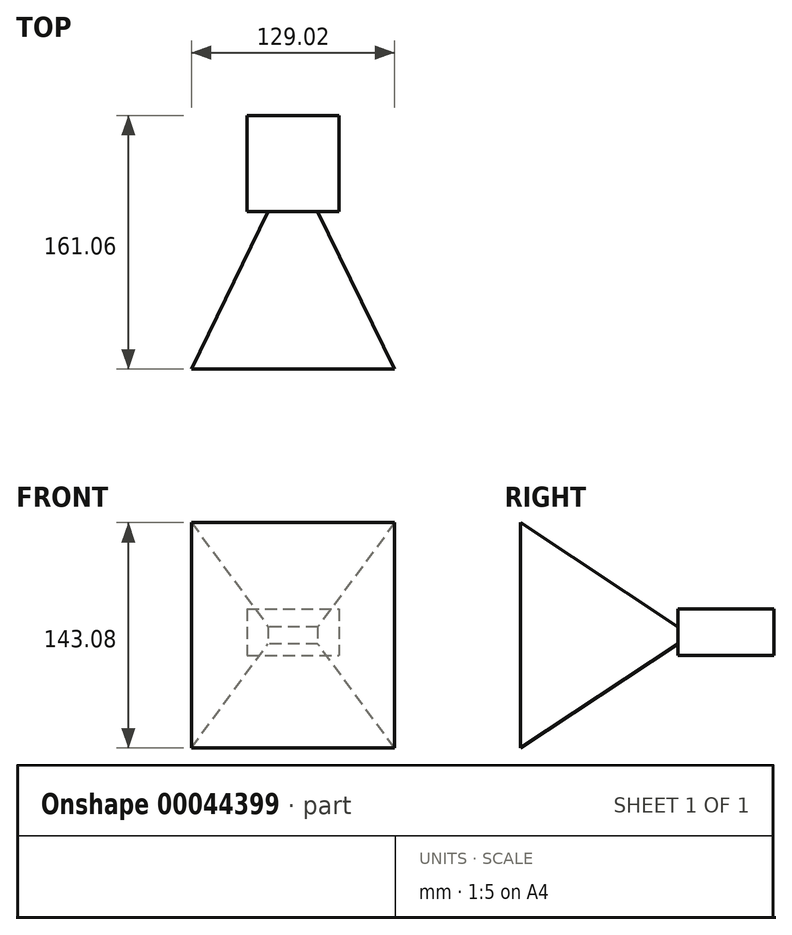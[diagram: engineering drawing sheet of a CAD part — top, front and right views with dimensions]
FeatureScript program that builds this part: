
annotation { "Feature Type Name" : "Feature", "Feature Type Description" : "" }
export const myFeature = defineFeature(function(context is Context, id is Id, definition is map)
    precondition{}
    {
        {
            var Q0;
            Q0=qCreatedBy(makeId("Top.planeOp"),FACE);
            cPlane(context, id + "F0", {"entities" : qUnion([Q0]), "cplaneType" : CPlaneType.OFFSET, "offset" : 12.64 * mm, "oppositeDirection" : true, "width" : 150 * mm, "height" : 150 * mm});
        }
        {
            var Q0;
            Q0=qCreatedBy(id+"F0.planeOp",FACE);
            var sketch = newSketch(context, id + "F1", { "sketchPlane" : qUnion([Q0])});
            skCircle(sketch, "E0", {"center": v(-15.77, 46.69) * mm, "radius": 1.5 * mm});
            skCircle(sketch, "E1", {"center": v(15.73, 16.46) * mm, "radius": 1.5 * mm});
            skLineSegment(sketch, "E2.bottom", {"start": v(-29.16, 61.06) * mm, "end": v(29.16, 61.06) * mm});
            skLineSegment(sketch, "E2.top", {"start": v(-29.16, 0) * mm, "end": v(29.16, 0) * mm});
            skLineSegment(sketch, "E2.left", {"start": v(-29.16, 61.06) * mm, "end": v(-29.16, 0) * mm});
            skLineSegment(sketch, "E2.right", {"start": v(29.16, 61.06) * mm, "end": v(29.16, 0) * mm});
            skPoint(sketch, "E3", {"position": v(0, 0) * mm});
            skSolve(sketch);
        }
        {
            var Q0;
            Q0=makeQuery(id+"F1.imprint","IMPRINT",FACE,{"disambiguationData":[TD([[makeQuery(id+"F1.imprint","IMPRINT",EDGE,{"derivedFrom":sQuery(id+"F1.wireOp",EDGE,"E0")}),-1.0]])]});
            var Q1;
            Q1=makeQuery(id+"F1.imprint","IMPRINT",FACE,{"disambiguationData":[TD([[makeQuery(id+"F1.imprint","IMPRINT",EDGE,{"derivedFrom":sQuery(id+"F1.wireOp",EDGE,"E0")}),1.0]])]});
            var Q2;
            Q2=makeQuery(id+"F1.imprint","IMPRINT",FACE,{"disambiguationData":[TD([[makeQuery(id+"F1.imprint","IMPRINT",EDGE,{"derivedFrom":sQuery(id+"F1.wireOp",EDGE,"E1")}),1.0]])]});
            extrude(context, id + "F2", {"entities" : qUnion([Q0, Q1, Q2]), "depth" : 29.4 * mm});
        }
        {
            var Q0;
            Q0=makeQuery(id+"F2.opExtrude","SWEPT_FACE",FACE,{"disambiguationData":[OSD([sQuery(id+"F1.wireOp",EDGE,"E2.top")])]});
            var sketch = newSketch(context, id + "F3", { "sketchPlane" : qUnion([Q0])});
            skLineSegment(sketch, "E4.rect.bottom", {"start": v(15.73, 5.35) * mm, "end": v(-15.73, 5.35) * mm});
            skLineSegment(sketch, "E4.rect.top", {"start": v(15.73, -5.35) * mm, "end": v(-15.73, -5.35) * mm});
            skLineSegment(sketch, "E4.rect.left", {"start": v(15.73, 5.35) * mm, "end": v(15.73, -5.35) * mm});
            skLineSegment(sketch, "E4.rect.right", {"start": v(-15.73, 5.35) * mm, "end": v(-15.73, -5.35) * mm});
            skPoint(sketch, "E4.rect.middle", {"position": v(0, 0) * mm});
            skSolve(sketch);
        }
        {
            var Q0;
            Q0=makeQuery(id+"F2.opExtrude","CAP_FACE",FACE,{"disambiguationData":[OSD([sQuery(id+"F1.wireOp",EDGE,"E0"),sQuery(id+"F1.wireOp",EDGE,"E1"),sQuery(id+"F1.wireOp",EDGE,"E2.bottom"),sQuery(id+"F1.wireOp",EDGE,"E2.top"),sQuery(id+"F1.wireOp",EDGE,"E2.left"),sQuery(id+"F1.wireOp",EDGE,"E2.right")])],"isStart":false});
            var sketch = newSketch(context, id + "F4", { "sketchPlane" : qUnion([Q0])});
            skText(sketch, "E5", { "text": "this is \nthe bottom.", "fontName": "OpenSans-Regular.ttf"});
            const initialGuessF4  = {"E5": [-0.01787, 0.03768, 1, 0, 0.0049]};
            skSetInitialGuess(sketch, initialGuessF4);
            skSolve(sketch);
        }
        {
            var Q0;
            Q0=qCreatedBy(makeId("Front.planeOp"),FACE);
            cPlane(context, id + "F5", {"entities" : qUnion([Q0]), "cplaneType" : CPlaneType.OFFSET, "offset" : 100 * mm, "width" : 150 * mm, "height" : 150 * mm});
        }
        {
            var Q0;
            Q0=qCreatedBy(makeId("Top.planeOp"),FACE);
            var sketch = newSketch(context, id + "F6", { "sketchPlane" : qUnion([Q0])});
            skPoint(sketch, "E6.0", {"position": v(-15.73, 0) * mm});
            skPoint(sketch, "E6.1", {"position": v(15.73, 0) * mm});
            skLineSegment(sketch, "E7", {"start": v(-15.73, 0) * mm, "end": v(-64.5, -100) * mm});
            skLineSegment(sketch, "E8.MirrorCS", {"start": v(15.73, 0) * mm, "end": v(64.5, -100) * mm});
            skSolve(sketch);
        }
        {
            var Q0;
            Q0=qCreatedBy(makeId("Right.planeOp"),FACE);
            var sketch = newSketch(context, id + "F7", { "sketchPlane" : qUnion([Q0])});
            skPoint(sketch, "E9.0", {"position": v(0, 5.35) * mm});
            skLineSegment(sketch, "E10", {"start": v(0, 5.35) * mm, "end": v(-100, 71.54) * mm});
            skLineSegment(sketch, "E11.MirrorCS", {"start": v(0, -5.35) * mm, "end": v(-100, -71.54) * mm});
            skSolve(sketch);
        }
        {
            var Q0;
            Q0=qCreatedBy(id+"F5.planeOp",FACE);
            var sketch = newSketch(context, id + "F8", { "sketchPlane" : qUnion([Q0])});
            skLineSegment(sketch, "E12.bottom", {"start": v(-64.5, -71.54) * mm, "end": v(64.5, -71.54) * mm});
            skLineSegment(sketch, "E12.top", {"start": v(-64.5, 71.54) * mm, "end": v(64.5, 71.54) * mm});
            skLineSegment(sketch, "E12.left", {"start": v(-64.5, -71.54) * mm, "end": v(-64.5, 71.54) * mm});
            skLineSegment(sketch, "E12.right", {"start": v(64.5, -71.54) * mm, "end": v(64.5, 71.54) * mm});
            skSolve(sketch);
        }
        {
            var Q1;
            Q1=makeQuery(id+"F8.imprint","IMPRINT",FACE,{"disambiguationData":[TD([[makeQuery(id+"F8.imprint","IMPRINT",EDGE,{"derivedFrom":sQuery(id+"F8.wireOp",EDGE,"E12.bottom")}),1.0]])]});
            var Q2;
            Q2=makeQuery(id+"F3.imprint","IMPRINT",FACE,{"disambiguationData":[TD([[makeQuery(id+"F3.imprint","IMPRINT",EDGE,{"derivedFrom":sQuery(id+"F3.wireOp",EDGE,"E4.rect.bottom")}),1.0]])]});
            loft(context, id + "F9", {"operationType" : NewBodyOperationType.ADD, "sheetProfilesArray" : [{ "sheetProfileEntities" : qUnion([Q1]) }, { "sheetProfileEntities" : qUnion([Q2]) }]});
        }
    });
